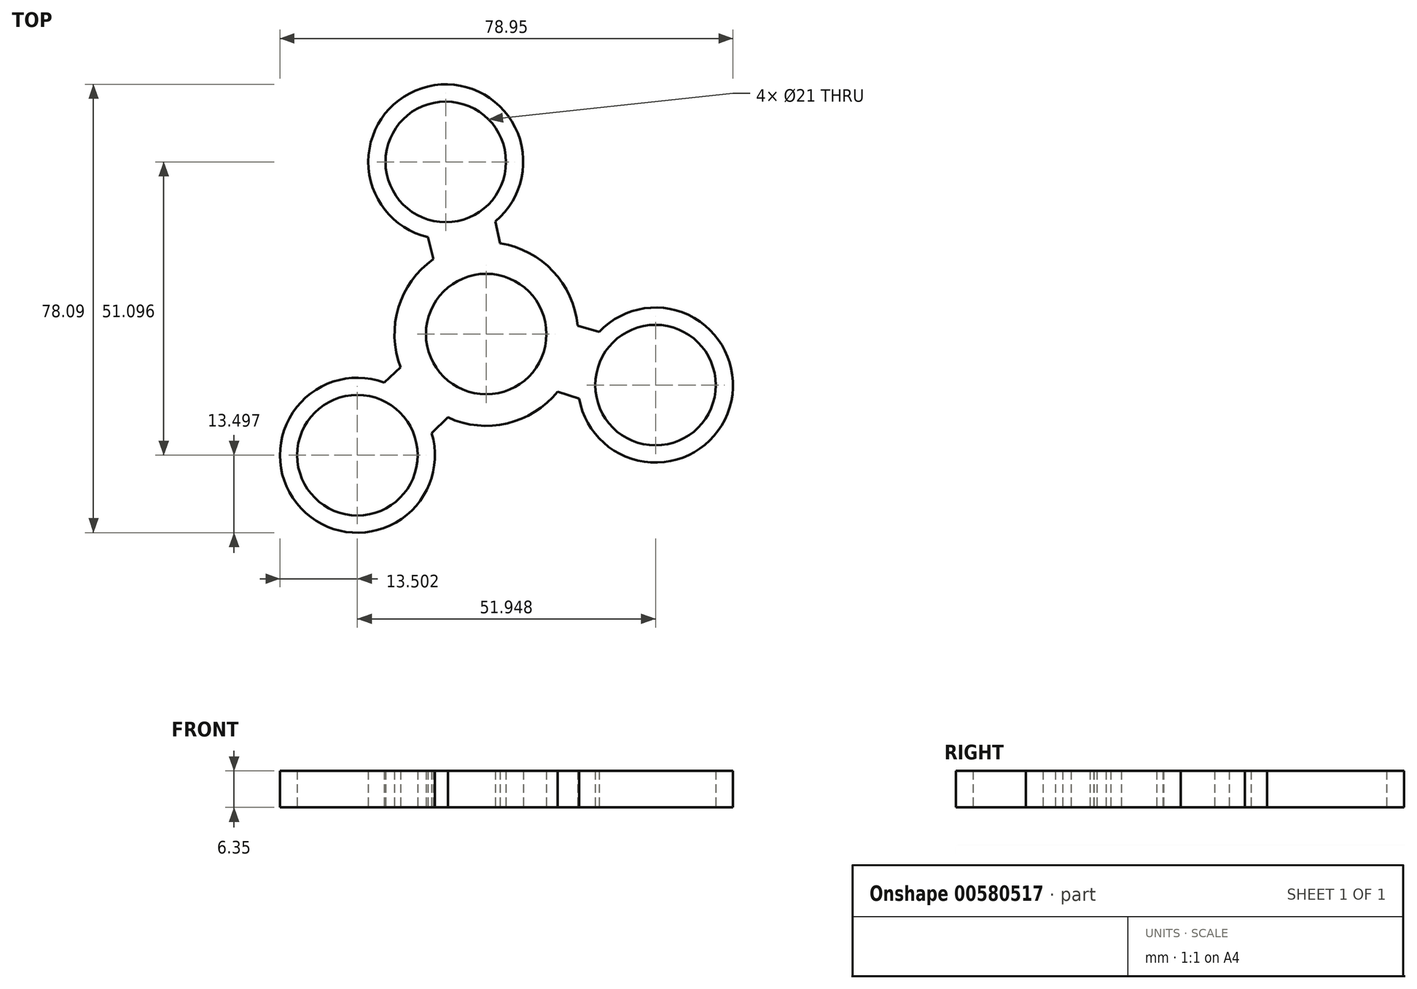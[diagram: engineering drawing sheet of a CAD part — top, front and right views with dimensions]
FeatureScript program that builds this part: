
annotation { "Feature Type Name" : "Feature", "Feature Type Description" : "" }
export const myFeature = defineFeature(function(context is Context, id is Id, definition is map)
    precondition{}
    {
        {
            var Q0;
            Q0=qCreatedBy(makeId("Top.planeOp"),FACE);
            var sketch = newSketch(context, id + "F0", { "sketchPlane" : qUnion([Q0])});
            skCircle(sketch, "E0", {"center": v(0, 0) * mm, "radius": 10.5 * mm});
            skArc(sketch, "E1", {"start": v(-6.69, -14.51) * mm, "mid": v(3.66, -15.55) * mm, "end": v(12.45, -10) * mm});
            skArc(sketch, "E2.trimOffspring", {"start": v(15.91, 1.46) * mm, "mid": v(11.64, 10.94) * mm, "end": v(2.44, 15.8) * mm});
            skArc(sketch, "E3.trimOffspring", {"start": v(-9.22, 13.05) * mm, "mid": v(-15.3, 4.61) * mm, "end": v(-14.9, -5.78) * mm});
            skLineSegment(sketch, "E4", {"start": v(-14.9, -5.78) * mm, "end": v(-17.81, -8.42) * mm});
            skLineSegment(sketch, "E5", {"start": v(-14.9, -5.78) * mm, "end": v(-6.69, -14.51) * mm});
            skLineSegment(sketch, "E6.MirrorCS", {"start": v(-6.69, -14.51) * mm, "end": v(-9.5, -17.26) * mm});
            skCircle(sketch, "E7", {"center": v(-22.45, -21.1) * mm, "radius": 10.5 * mm});
            skCircle(sketch, "E8", {"center": v(-22.45, -21.1) * mm, "radius": 13.5 * mm});
            skCircle(sketch, "E9.1.0", {"center": v(29.5, -8.89) * mm, "radius": 13.5 * mm});
            skCircle(sketch, "E9.1.1", {"center": v(29.5, -8.89) * mm, "radius": 10.5 * mm});
            skLineSegment(sketch, "E9.1.2", {"start": v(15.91, 1.46) * mm, "end": v(19.7, 0.4) * mm});
            skLineSegment(sketch, "E9.1.3", {"start": v(12.45, -10) * mm, "end": v(16.2, -11.21) * mm});
            skCircle(sketch, "E9.2.0", {"center": v(-7.05, 30) * mm, "radius": 13.5 * mm});
            skCircle(sketch, "E9.2.1", {"center": v(-7.05, 30) * mm, "radius": 10.5 * mm});
            skLineSegment(sketch, "E9.2.2", {"start": v(-9.22, 13.05) * mm, "end": v(-10.2, 16.86) * mm});
            skLineSegment(sketch, "E9.2.3", {"start": v(2.44, 15.8) * mm, "end": v(1.6, 19.64) * mm});
            skSolve(sketch);
        }
        {
            var Q0;
            Q0=makeQuery(id+"F0.imprint","IMPRINT",FACE,{"disambiguationData":[TD([[makeQuery(id+"F0.imprint","IMPRINT",EDGE,{"derivedFrom":sQuery(id+"F0.wireOp",EDGE,"E9.2.1")}),-1.0]])]});
            var Q1;
            Q1=makeQuery(id+"F0.imprint","IMPRINT",FACE,{"disambiguationData":[TD([[makeQuery(id+"F0.imprint","IMPRINT",EDGE,{"derivedFrom":sQuery(id+"F0.wireOp",EDGE,"E0")}),-1.0]])]});
            var Q2;
            {var subQ0=sQuery(id+"F0.wireOp",EDGE,"E4");Q2=makeQuery(id+"F0.imprint","IMPRINT",FACE,{"disambiguationData":[TD([[makeQuery(id+"F0.imprint","IMPRINT",EDGE,{"derivedFrom":subQ0}),1.0]])]});}
            var Q3;
            Q3=makeQuery(id+"F0.imprint","IMPRINT",FACE,{"disambiguationData":[TD([[makeQuery(id+"F0.imprint","IMPRINT",EDGE,{"derivedFrom":sQuery(id+"F0.wireOp",EDGE,"E9.1.1")}),-1.0]])]});
            var Q4;
            Q4=makeQuery(id+"F0.imprint","IMPRINT",FACE,{"disambiguationData":[TD([[makeQuery(id+"F0.imprint","IMPRINT",EDGE,{"derivedFrom":sQuery(id+"F0.wireOp",EDGE,"E7")}),-1.0]])]});
            extrude(context, id + "F1", {"entities" : qUnion([Q0, Q1, Q2, Q3, Q4]), "depth" : 6.35 * mm, "offsetDistance" : 25 * mm});
        }
    });
